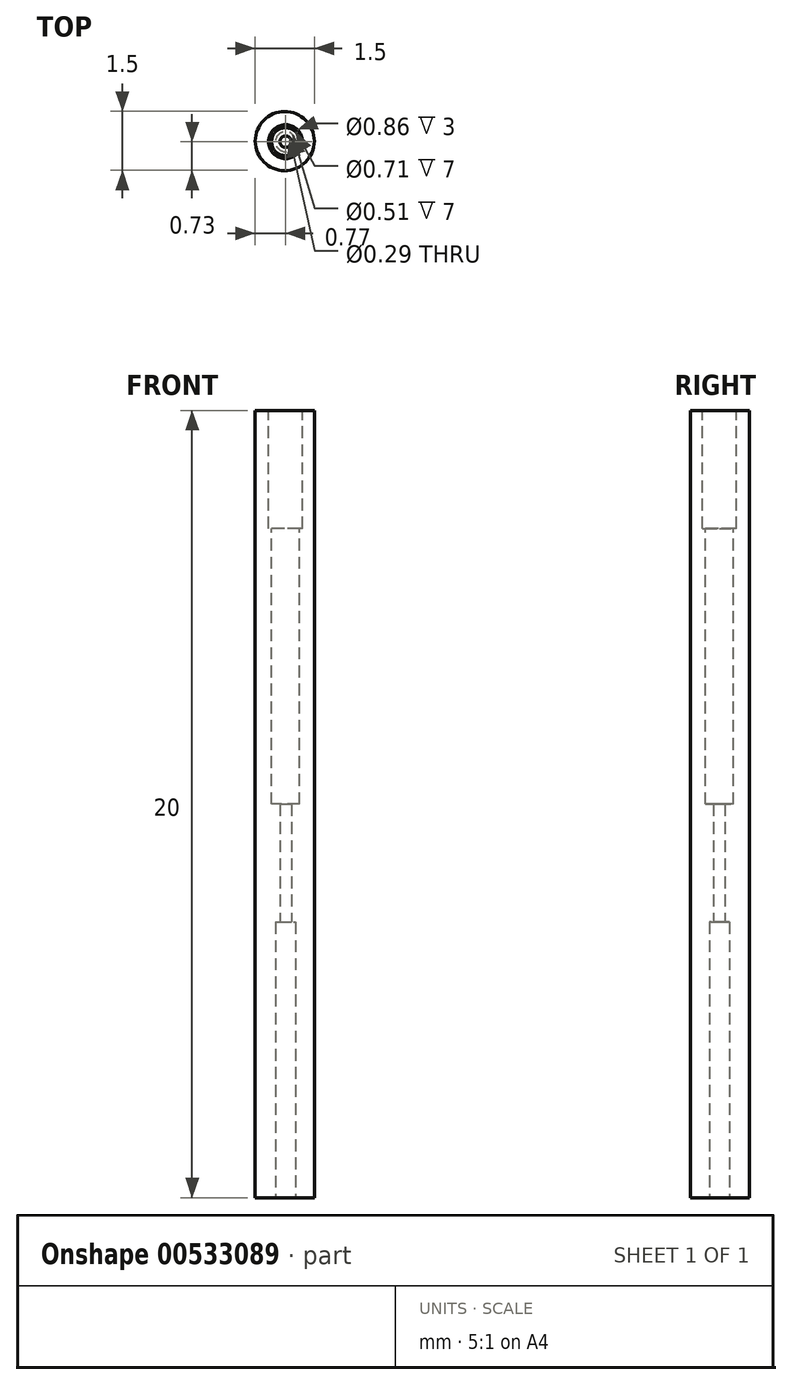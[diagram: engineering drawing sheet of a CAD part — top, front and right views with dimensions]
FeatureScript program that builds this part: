
annotation { "Feature Type Name" : "Feature", "Feature Type Description" : "" }
export const myFeature = defineFeature(function(context is Context, id is Id, definition is map)
    precondition{}
    {
        {
            var Q0;
            Q0=qCreatedBy(makeId("Top.planeOp"),FACE);
            var sketch = newSketch(context, id + "F0", { "sketchPlane" : qUnion([Q0])});
            skCircle(sketch, "E0", {"center": v(-0.02, 0.02) * mm, "radius": 0.75 * mm});
            skSolve(sketch);
        }
        {
            var Q0;
            Q0 = qSketchRegion(id + "F0", true);
            extrude(context, id + "F1", {"entities" : qUnion([Q0]), "depth" : 20 * mm, "offsetDistance" : 25 * mm});
        }
        {
            var Q0;
            Q0=makeQuery(id+"F1.opExtrude","CAP_FACE",FACE,{"disambiguationData":[OSD([sQuery(id+"F0.wireOp",EDGE,"E0")])],"isStart":false});
            var sketch = newSketch(context, id + "F2", { "sketchPlane" : qUnion([Q0])});
            skCircle(sketch, "E1", {"center": v(0, 0) * mm, "radius": 0.43 * mm});
            skSolve(sketch);
        }
        {
            var Q0;
            Q0 = qSketchRegion(id + "F2", true);
            extrude(context, id + "F3", {"entities" : qUnion([Q0]), "operationType" : NewBodyOperationType.REMOVE, "oppositeDirection" : true, "depth" : 3 * mm, "offsetDistance" : 25 * mm});
        }
        {
            var Q0;
            Q0=makeQuery(id+"F3.boolean.opBoolean","COPY",FACE,{"derivedFrom":makeQuery(id+"F3.opExtrude","CAP_FACE",FACE,{"disambiguationData":[OSD([sQuery(id+"F2.wireOp",EDGE,"E1")])],"isStart":false})});
            var sketch = newSketch(context, id + "F4", { "sketchPlane" : qUnion([Q0])});
            skCircle(sketch, "E2", {"center": v(0, 0) * mm, "radius": 0.36 * mm});
            skSolve(sketch);
        }
        {
            var Q0;
            Q0 = qSketchRegion(id + "F4", true);
            extrude(context, id + "F5", {"entities" : qUnion([Q0]), "operationType" : NewBodyOperationType.REMOVE, "oppositeDirection" : true, "depth" : 7 * mm, "offsetDistance" : 25 * mm});
        }
        {
            var Q0;
            Q0=makeQuery(id+"F1.opExtrude","CAP_FACE",FACE,{"disambiguationData":[OSD([sQuery(id+"F0.wireOp",EDGE,"E0")])],"isStart":true});
            var sketch = newSketch(context, id + "F6", { "sketchPlane" : qUnion([Q0])});
            skCircle(sketch, "E3", {"center": v(0, 0) * mm, "radius": 0.25 * mm});
            skSolve(sketch);
        }
        {
            var Q0;
            Q0 = qSketchRegion(id + "F6", true);
            extrude(context, id + "F7", {"entities" : qUnion([Q0]), "operationType" : NewBodyOperationType.REMOVE, "oppositeDirection" : true, "depth" : 7 * mm, "offsetDistance" : 25 * mm});
        }
        {
            var Q0;
            Q0=makeQuery(id+"F7.boolean.opBoolean","COPY",FACE,{"derivedFrom":makeQuery(id+"F7.opExtrude","CAP_FACE",FACE,{"disambiguationData":[OSD([sQuery(id+"F6.wireOp",EDGE,"E3")])],"isStart":false})});
            var sketch = newSketch(context, id + "F8", { "sketchPlane" : qUnion([Q0])});
            skCircle(sketch, "E4", {"center": v(0, 0) * mm, "radius": 0.15 * mm});
            skSolve(sketch);
        }
        {
            var Q0;
            Q0 = qSketchRegion(id + "F8", true);
            extrude(context, id + "F9", {"entities" : qUnion([Q0]), "operationType" : NewBodyOperationType.REMOVE, "oppositeDirection" : true, "depth" : 3 * mm, "offsetDistance" : 25 * mm});
        }
    });
